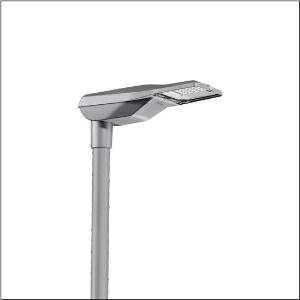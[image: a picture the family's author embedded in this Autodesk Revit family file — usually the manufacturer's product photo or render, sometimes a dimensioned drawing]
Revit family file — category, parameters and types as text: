
# Revit family: streetlight_sl_21_micro___st1_0a_5xe5d33a08cb_e1ea
name_source: partatom
category: Lighting Fixtures
units: mm (PartAtom-declared; Revit-internal decimal feet)

## family parameters
Cut with Voids When Loaded = No
Host = Face
Light Source = No
Part Type = Normal
Room Calculation Point = No
Round Connector Dimension = Use Diameter
Shared = No

## types (1)
- --- (1 x LED, 2290 lm, 15.8 W, 3000K)
    Apparent Load = 16 VA
    CIE Flux Codes = 37 72 97 100 100
    Color Rendering = 70
    Color Temperature = 3000K
    Default Elevation = 1800 mm
    Description = Streetlight SL 21 micro, mast luminaire, primary light control with lens, of PMMA, primary optical cover: cover, of toughened safety glass, transparent, light distribution: ST1.0a, light emission: direct distribution, primary light characteristic: asymmetric, installation type: side-entry, post-top, LED, 3G 1.5mm², High Power LED, rated luminous flux: 2.290lm, luminous efficacy: 145lm/W, light colour: 730, colour temperature: 3000K, control: flexible luminous flux parameterisation, time-dependent luminous flux control, constant luminous flux control, overheat protection, mains connection: 230..240V, AC, 50/60Hz, connection cable pre-assembled, cable length: 5,5m, wiring characteristics: H07RN-F, start of lifetime: 16W, end of service life: 16W, reduction: 9W, luminaire housing, of diecast aluminium, powder-coated, Siteco® metallic grey (DB 702S), corrosivity category C5 mid according to DIN EN ISO 12944, please order mast flange separately, inclination adjustable: 0°, 5°, 10°, 15°, sealing non-destructively replaceable, multi-level sealing system, length: 528mm, width: 235mm, height: 110mm, mast flange for spigot size: 42mm (side-entry): 5XC10008XM4, 60/48mm (side-entry/post-top): 5XC10108XM2, 76/60mm (side-entry/post-top): 5XC10108XM1, protection rating (complete): IP66, insulation class (complete): insulation class II (safety insulation), certification: CE, ENEC, ENEC+, VDE, impact resistance: IK09, permissible operating ambient temperature for outdoor applications: -40..+50°C, standard-compliant lighting for roads and squares, packaging unit: 1 piece

Light Distribution: ST1.0a
    Height = 110 mm
    Lamp = 1 x LED
    Lamp Light Flux = 2290 lm
    Lamp Power = 15.8 W
    Lamp count = 1
    Length = 528 mm
    Luminous efficacy = 145 lm/W
    Manufacturer = Siteco
    ModVariant = No
    Model = 5XE5D33A08CB
    Number of Poles = 1
    OnlyDefault = Yes
    Power Factor = 1
    Product Name = Streetlight SL 21 micro | ST1.0a
    Product group = mast luminaire | pylon top
    ProductGroupID = 6100
    Protection Class = Protection class II
    Protection Degree = IP 66
    RLX_Detail_Level = 1
    RLX_Emergency_Light_Flux = 0 lm
    RLX_Emergency_Type = 0
    RLX_Emergency_Type_DB = No
    RlxData = <blob elided: 98081 chars, md5=71eac9c8>
    Socket = socket
    Standby Power = 0 W
    System Light Flux = 2290 lm
    System Power = 16 W
    Type Comments = factory setting: luminous flux: 100 % | Output Level: 100 % | 300 mA
    Type Image = l_1006881.jpg
    URL = http://relux.com
    VarID = @adj_105821
    Voltage = 0 V
    Weight = 0.00 kg
    Width = 235 mm

## geometry (parser evidence)
native form markers: Blend x4, Sweep x10
no freeform markers — native parametric forms only
